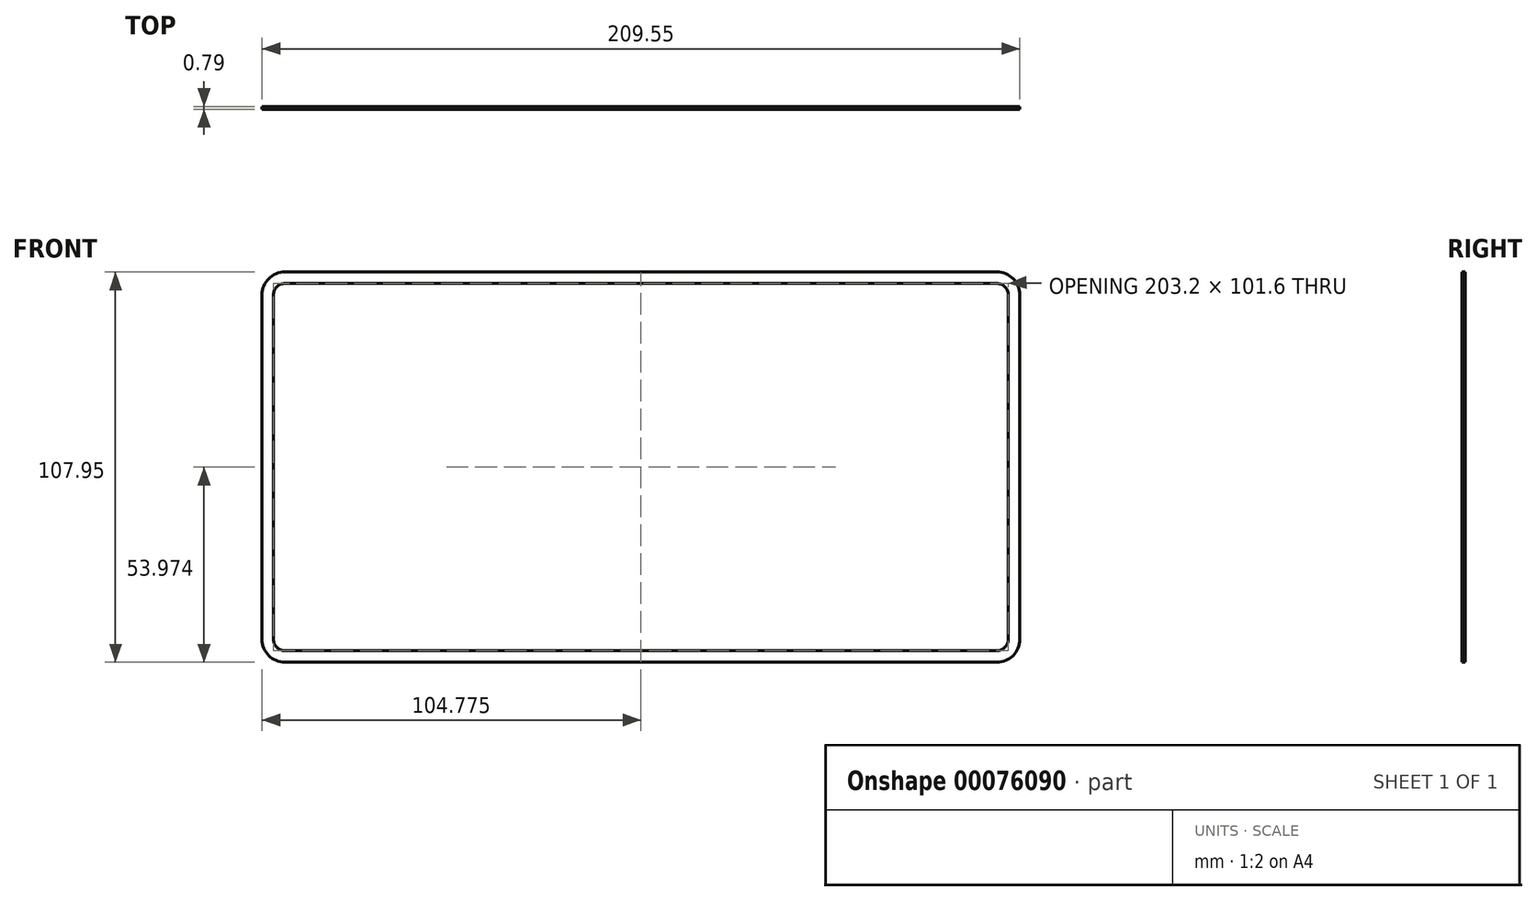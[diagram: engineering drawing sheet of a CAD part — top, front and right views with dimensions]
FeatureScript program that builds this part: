
annotation { "Feature Type Name" : "Feature", "Feature Type Description" : "" }
export const myFeature = defineFeature(function(context is Context, id is Id, definition is map)
    precondition{}
    {
        {
            var Q0;
            Q0=qCreatedBy(makeId("Front.planeOp"),FACE);
            var sketch = newSketch(context, id + "F0", { "sketchPlane" : qUnion([Q0])});
            skLineSegment(sketch, "E0.bottom", {"start": v(-100.18, 56.7) * mm, "end": v(96.67, 56.7) * mm});
            skLineSegment(sketch, "E0.top", {"start": v(-100.18, -51.25) * mm, "end": v(96.67, -51.25) * mm});
            skLineSegment(sketch, "E0.left", {"start": v(-106.53, 50.35) * mm, "end": v(-106.53, -44.9) * mm});
            skLineSegment(sketch, "E0.right", {"start": v(103.02, 50.35) * mm, "end": v(103.02, -44.9) * mm});
            skPoint(sketch, "E1.visualSharp", {"position": v(-106.53, 56.7) * mm});
            skArc(sketch, "E1.filletArc", {"start": v(-100.18, 56.7) * mm, "mid": v(-104.67, 54.84) * mm, "end": v(-106.53, 50.35) * mm});
            skPoint(sketch, "E2.visualSharp", {"position": v(-106.53, -51.25) * mm});
            skArc(sketch, "E2.filletArc", {"start": v(-106.53, -44.9) * mm, "mid": v(-104.67, -49.4) * mm, "end": v(-100.18, -51.25) * mm});
            skPoint(sketch, "E3.visualSharp", {"position": v(103.02, -51.25) * mm});
            skArc(sketch, "E3.filletArc", {"start": v(96.67, -51.25) * mm, "mid": v(101.16, -49.4) * mm, "end": v(103.02, -44.9) * mm});
            skPoint(sketch, "E4.visualSharp", {"position": v(103.02, 56.7) * mm});
            skArc(sketch, "E4.filletArc", {"start": v(103.02, 50.35) * mm, "mid": v(101.16, 54.84) * mm, "end": v(96.67, 56.7) * mm});
            skArc(sketch, "E5.0", {"start": v(-100.18, 53.52) * mm, "mid": v(-102.42, 52.6) * mm, "end": v(-103.35, 50.35) * mm});
            skLineSegment(sketch, "E5.1", {"start": v(-103.35, 50.35) * mm, "end": v(-103.35, -44.9) * mm});
            skLineSegment(sketch, "E5.2", {"start": v(-100.18, 53.52) * mm, "end": v(96.67, 53.52) * mm});
            skArc(sketch, "E5.3", {"start": v(-103.35, -44.9) * mm, "mid": v(-102.42, -47.15) * mm, "end": v(-100.18, -48.08) * mm});
            skArc(sketch, "E5.4", {"start": v(99.85, 50.35) * mm, "mid": v(98.92, 52.6) * mm, "end": v(96.67, 53.52) * mm});
            skLineSegment(sketch, "E5.5", {"start": v(99.85, 50.35) * mm, "end": v(99.85, -44.9) * mm});
            skArc(sketch, "E5.6", {"start": v(96.67, -48.08) * mm, "mid": v(98.92, -47.15) * mm, "end": v(99.85, -44.9) * mm});
            skLineSegment(sketch, "E5.7", {"start": v(-100.18, -48.08) * mm, "end": v(96.67, -48.08) * mm});
            skSolve(sketch);
        }
        {
            var Q0;
            Q0 = qSketchRegion(id + "F0", true);
            extrude(context, id + "F1", {"entities" : qUnion([Q0]), "depth" : 0.8 * mm});
        }
    });
